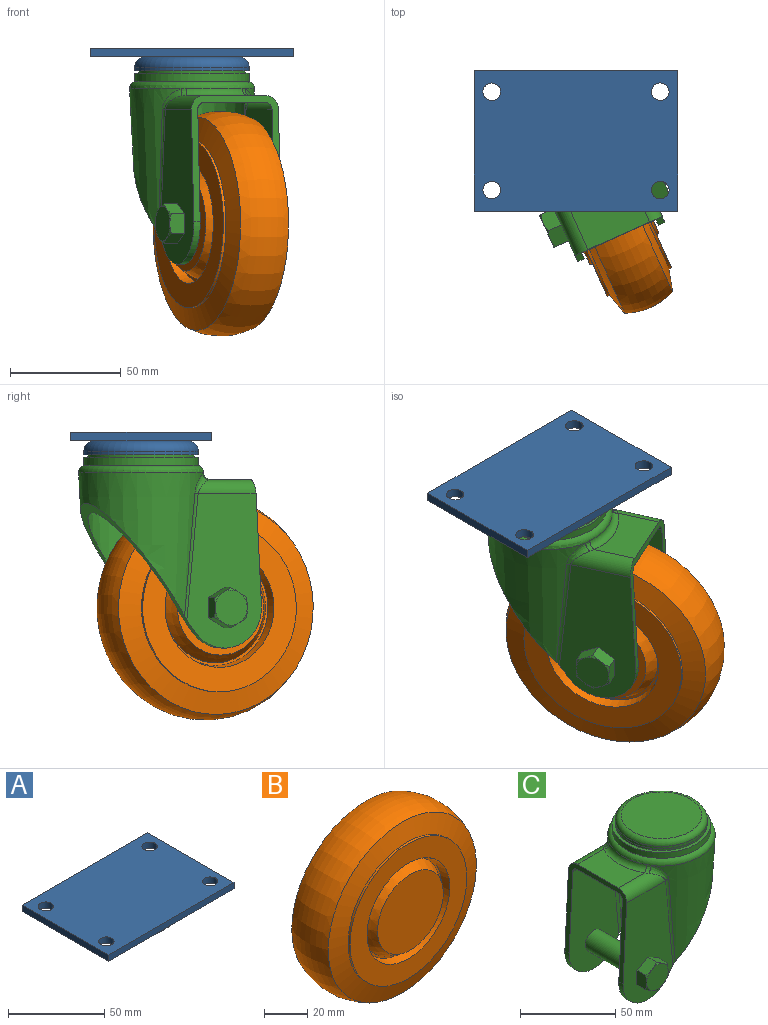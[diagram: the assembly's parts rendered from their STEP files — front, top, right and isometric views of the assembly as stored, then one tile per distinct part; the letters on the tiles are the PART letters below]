
ASSEMBLY  parts=3 mates=2
PART A: 16 faces, bbox 92.1x63.5x10.3 mm
  f0: plane 42.29x42.29mm, normal (0,0,-1), area 1404.7mm2, adj f1
  f1: torus R=21.15mm, axis (0,0,1), area 678.8mm2, adj f0,f2
  f2: cylinder r=24.13mm len=48.26mm, axis (0,0,1), area 231.1mm2, adj f1,f15
  f3: plane 92.08x63.5mm, normal (0,0,1), area 5648.8mm2, adj f4,f5,f6,f7,f8,f9,f10,f11
  f4: cylinder r=3.97mm len=7.94mm, axis (0,0,1), area 99mm2, adj f3,f12
  f5: cylinder r=3.97mm len=7.94mm, axis (0,0,1), area 99mm2, adj f3,f12
  f6: cylinder r=3.97mm len=7.94mm, axis (0,0,1), area 99mm2, adj f3,f12
  f7: cylinder r=3.97mm len=7.94mm, axis (0,0,1), area 99mm2, adj f3,f12
  f8: plane 92.08x3.97mm, normal (0,-1,0), area 365.4mm2, adj f3,f9,f11,f12
  f9: plane 63.5x3.97mm, normal (1,0,0), area 252mm2, adj f3,f8,f10,f12
  f10: plane 92.08x3.97mm, normal (0,1,0), area 365.4mm2, adj f3,f9,f11,f12
  f11: plane 63.5x3.97mm, normal (-1,0,0), area 252mm2, adj f3,f8,f10,f12
  f12: plane 92.08x63.5mm, normal (0,0,-1), area 4244.1mm2, adj f4,f5,f6,f7,f8,f9,f10,f11
  f13: torus R=21.15mm, axis (0,0,1), area 1136.4mm2, adj f12,f14
  f14: cylinder r=25.91mm len=51.82mm, axis (0,0,1), area 248.1mm2, adj f13,f15
  f15: plane 51.82x51.82mm, normal (0,0,-1), area 279.5mm2, adj f2,f14
PART B: 15 faces, bbox 101.6x34.3x96.5 mm
  f0: cone r=21.43mm half-angle=30deg, axis (0,-1,0), area 1014.2mm2, adj f13,f14
  f1: cone r=26.15mm half-angle=10deg, axis (0,1,0), area 807.3mm2, adj f12,f13
  f2: cylinder r=38.1mm len=76.2mm, axis (0,1,0), area 304mm2, adj f3,f12
  f3: cone r=38.1mm half-angle=75deg, axis (0,-1,0), area 2853.7mm2, adj f2,f4
  f4: torus R=21.74mm, axis (0,1,0), area 7683.5mm2, adj f3,f5
  f5: cone r=48.26mm half-angle=75deg, axis (0,1,0), area 2853.7mm2, adj f4,f6
  f6: cylinder r=38.1mm len=76.2mm, axis (0,1,0), area 304mm2, adj f5,f11
  f7: cone r=26.99mm half-angle=10deg, axis (0,-1,0), area 807.3mm2, adj f10,f11
  f8: cone r=24.91mm half-angle=30deg, axis (0,1,0), area 1014.2mm2, adj f9,f10
  f9: plane 42.86x42.86mm, normal (0,-1,0), area 1442.9mm2, adj f8
  f10: plane 52.3x52.3mm, normal (0,-1,0), area 197.9mm2, adj f7,f8
  f11: plane 76.2x76.2mm, normal (0,-1,0), area 2272.3mm2, adj f6,f7
  f12: plane 76.2x76.2mm, normal (0,1,0), area 2272.3mm2, adj f1,f2
  f13: plane 52.3x52.3mm, normal (0,1,0), area 197.9mm2, adj f0,f1
  f14: plane 42.86x42.86mm, normal (0,1,0), area 1442.9mm2, adj f0
PART C: 66 faces, bbox 81.4x62x92.6 mm
  f0: cylinder r=6.35mm len=36.83mm, axis (0,1,0), area 1469.5mm2, adj f12,f13
  f1: cone r=25.28mm half-angle=3deg, axis (0,0,1), area 3946.1mm2, adj f25,f29,f30,f31,f32,f33
  f2: cylinder r=18.26mm len=32.74mm, axis (0,1,0), area 147.2mm2, adj f11,f13,f24,f25
  f3: cylinder r=18.26mm len=32.74mm, axis (0,1,0), area 147.2mm2, adj f10,f12,f24,f25
  f4: torus R=25.1mm, axis (0,0,-1), area 874.3mm2, adj f5,f8,f20,f21,f22
  f5: cone r=28.45mm half-angle=3deg, axis (0,0,1), area 4250.8mm2, adj f4,f17,f18,f19,f23,f25
  f6: cylinder r=25.91mm len=51.82mm, axis (0,0,1), area 598.5mm2, adj f8,f9
  f7: cylinder r=24.13mm len=48.26mm, axis (0,0,1), area 173.3mm2, adj f9,f65
  f8: plane 51.82x51.82mm, normal (0,0,-1), area 129.1mm2, adj f4,f6
  f9: plane 51.82x51.82mm, normal (0,0,1), area 279.5mm2, adj f6,f7
  f10: plane 69.86x37.01mm, normal (0,1,0), area 1987.2mm2, adj f3,f16,f17,f24,f25,f50,f51,f52
  f11: plane 69.86x37.01mm, normal (0,-1,0), area 1987.2mm2, adj f2,f15,f18,f24,f25,f37,f38,f39
  f12: plane 69.86x37.01mm, normal (0,-1,0), area 2078.8mm2, adj f0,f3,f24,f25,f33,f34
  f13: plane 69.86x37.01mm, normal (0,1,0), area 2078.8mm2, adj f0,f2,f24,f25,f32,f35
  f14: plane 30.48x19.48mm, normal (0,0,1), area 512.7mm2, adj f15,f16,f21,f24
  f15: cylinder r=6.35mm len=28.74mm, axis (1,0,0), area 240.7mm2, adj f11,f14,f22,f23,f24
  f16: cylinder r=6.35mm len=28.74mm, axis (-1,0,0), area 240.7mm2, adj f10,f14,f19,f20,f24
  f17: bspline ~57.31x7.06mm, area 103mm2, adj f5,f10,f19,f25
  f18: bspline ~57.31x7.06mm, area 103mm2, adj f5,f11,f23,f25
  f19: bspline ~9.36x9.29mm, area 39.7mm2, adj f5,f16,f17,f20
  f20: bspline ~4.17x3.4mm, area 11.1mm2, adj f4,f16,f19,f21
  f21: torus R=31.45mm, axis (0,0,-1), area 148.5mm2, adj f4,f14,f20,f22
  f22: bspline ~4.17x3.4mm, area 11.1mm2, adj f4,f15,f21,f23
  f23: bspline ~9.36x9.29mm, area 39.7mm2, adj f5,f15,f18,f22
  f24: plane 57.23x43.41mm, normal (-1,0,0.05), area 466.5mm2, adj f2,f3,f10,f11,f12,f13,f14,f15
  f25: plane 58.77x58.5mm, normal (0.79,0,-0.61), area 618.5mm2, adj f1,f2,f3,f5,f10,f11,f12,f13
  f26: torus R=31.45mm, axis (0,0,-1), area 276.6mm2, adj f27,f28,f29,f36
  f27: bspline ~6.78x6.46mm, area 16.1mm2, adj f26,f29,f31,f35
  f28: bspline ~6.78x6.46mm, area 16.1mm2, adj f26,f29,f30,f34
  f29: plane 50.22x50.22mm, normal (0,0,-1), area 1979.6mm2, adj f1,f26,f27,f28
  f30: bspline ~11.19x9.53mm, area 63.5mm2, adj f1,f28,f33,f34
  f31: bspline ~11.19x9.53mm, area 63.5mm2, adj f1,f27,f32,f35
  f32: bspline ~57.82x8.57mm, area 203.4mm2, adj f1,f13,f25,f31
  f33: bspline ~57.82x8.57mm, area 203.4mm2, adj f1,f12,f25,f30
  f34: cylinder r=3.17mm len=28.74mm, axis (-1,0,0), area 120.8mm2, adj f12,f24,f28,f30,f36
  f35: cylinder r=3.17mm len=28.74mm, axis (1,0,0), area 120.8mm2, adj f13,f24,f27,f31,f36
  f36: plane 30.48x19.65mm, normal (0,0,-1), area 517.8mm2, adj f24,f26,f34,f35
  f37: plane 8.69x7.99mm, normal (-0.5,0,-0.87), area 64.1mm2, adj f11,f38,f42,f44,f45
  f38: plane 8.69x7.99mm, normal (0.5,0,-0.87), area 64.1mm2, adj f11,f37,f39,f43,f44
  f39: plane 9.92x8mm, normal (1,0,0), area 64.1mm2, adj f11,f38,f40,f43,f48
  f40: plane 8.69x7.99mm, normal (0.5,0,0.87), area 64.1mm2, adj f11,f39,f41,f47,f48
  f41: plane 8.69x7.99mm, normal (-0.5,0,0.87), area 64.1mm2, adj f11,f40,f42,f46,f47
  f42: plane 9.92x8mm, normal (-1,0,0), area 64.1mm2, adj f11,f37,f41,f45,f46
  f43: cone r=7.94mm half-angle=60deg, axis (0,1,0), area 6.2mm2, adj f38,f39,f49
  f44: cone r=7.94mm half-angle=60deg, axis (0,1,0), area 6.2mm2, adj f37,f38,f49
  f45: cone r=7.94mm half-angle=60deg, axis (0,1,0), area 6.2mm2, adj f37,f42,f49
  f46: cone r=7.94mm half-angle=60deg, axis (0,1,0), area 6.2mm2, adj f41,f42,f49
  f47: cone r=7.94mm half-angle=60deg, axis (0,1,0), area 6.2mm2, adj f40,f41,f49
  f48: cone r=7.94mm half-angle=60deg, axis (0,1,0), area 6.2mm2, adj f39,f40,f49
  f49: plane 15.88x15.88mm, normal (0,-1,0), area 197.9mm2, adj f43,f44,f45,f46,f47,f48
  f50: plane 8.69x7.99mm, normal (-0.5,0,-0.87), area 64.1mm2, adj f10,f51,f55,f57,f58
  f51: plane 8.69x7.99mm, normal (0.5,0,-0.87), area 64.1mm2, adj f10,f50,f52,f56,f57
  f52: plane 9.92x8mm, normal (1,0,0), area 64.1mm2, adj f10,f51,f53,f56,f61
  f53: plane 8.69x7.99mm, normal (0.5,0,0.87), area 64.1mm2, adj f10,f52,f54,f60,f61
  f54: plane 8.69x7.99mm, normal (-0.5,0,0.87), area 64.1mm2, adj f10,f53,f55,f59,f60
  f55: plane 9.92x8mm, normal (-1,0,0), area 64.1mm2, adj f10,f50,f54,f58,f59
  f56: cone r=7.94mm half-angle=60deg, axis (0,-1,0), area 6.2mm2, adj f51,f52,f62
  f57: cone r=7.94mm half-angle=60deg, axis (0,-1,0), area 6.2mm2, adj f50,f51,f62
  f58: cone r=7.94mm half-angle=60deg, axis (0,-1,0), area 6.2mm2, adj f50,f55,f62
  f59: cone r=7.94mm half-angle=60deg, axis (0,-1,0), area 6.2mm2, adj f54,f55,f62
  f60: cone r=7.94mm half-angle=60deg, axis (0,-1,0), area 6.2mm2, adj f53,f54,f62
  f61: cone r=7.94mm half-angle=60deg, axis (0,-1,0), area 6.2mm2, adj f52,f53,f62
  f62: plane 15.88x15.88mm, normal (0,1,0), area 197.9mm2, adj f56,f57,f58,f59,f60,f61
  f63: plane 42.29x42.29mm, normal (0,0,1), area 1404.7mm2, adj f64
  f64: torus R=21.15mm, axis (0,0,1), area 678.8mm2, adj f63,f65
  f65: cylinder r=24.13mm len=48.26mm, axis (0,0,1), area 231.1mm2, adj f7,f64
PLACE A at identity
PLACE B rot(axis=(0.81,-0.53,0.24),162.1deg) t=(41.77,-92.87,-128.33)mm
PLACE C rot(axis=(0,0,1),114.2deg) t=(0,0,0)mm
MATE revolute C.f64 <-> A.f1  axis (0,0,1) through (0,0,-5.75)mm
MATE revolute B.f0 <-> C.f56  axis (-0.91,-0.41,0) through (13.02,-28.96,-79.38)mm
